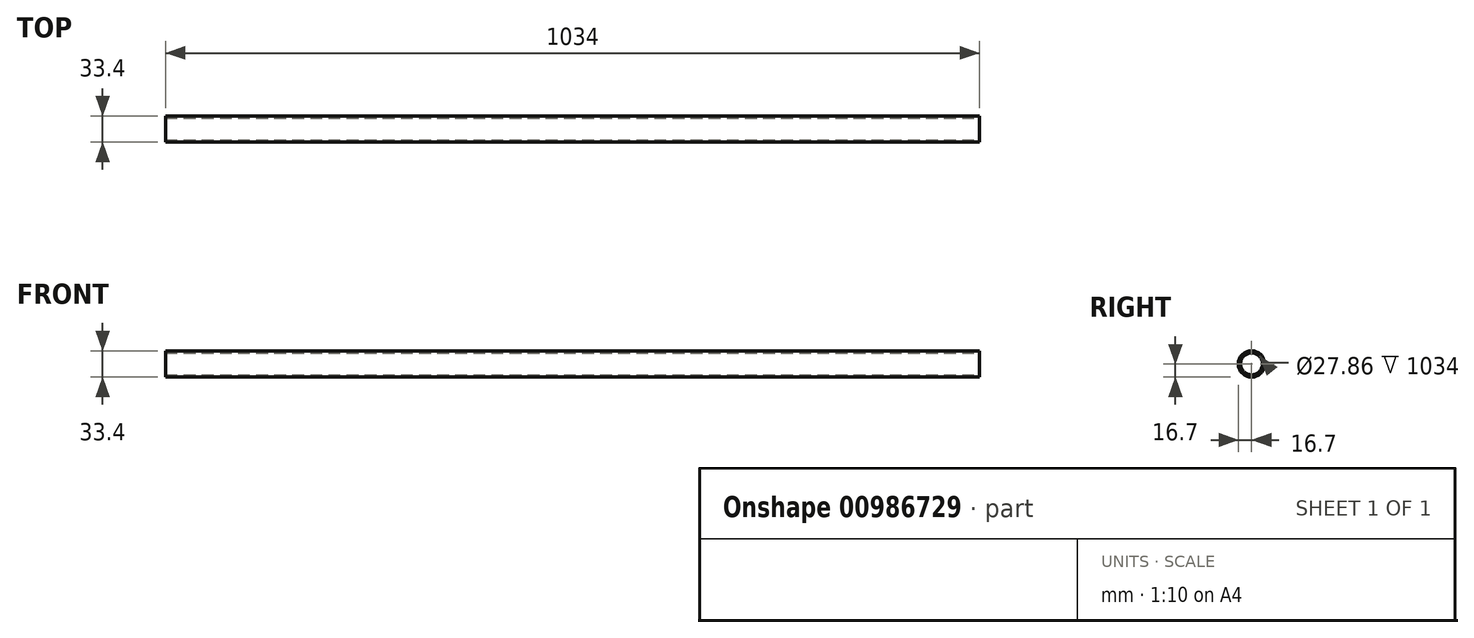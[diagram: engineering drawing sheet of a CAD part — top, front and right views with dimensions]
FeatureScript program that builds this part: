
annotation { "Feature Type Name" : "Feature", "Feature Type Description" : "" }
export const myFeature = defineFeature(function(context is Context, id is Id, definition is map)
    precondition{}
    {
        {
            var Q0;
            Q0=qCreatedBy(makeId("Front.planeOp"),FACE);
            var sketch = newSketch(context, id + "F0", { "sketchPlane" : qUnion([Q0])});
            skLineSegment(sketch, "E0", {"start": v(0, 0) * mm, "end": v(1034, 0) * mm});
            skSolve(sketch);
        }
        {
            var Q0;
            Q0=qCreatedBy(makeId("Right.planeOp"),FACE);
            var sketch = newSketch(context, id + "F1", { "sketchPlane" : qUnion([Q0])});
            skCircle(sketch, "E1", {"center": v(0, 0) * mm, "radius": 16.7 * mm});
            skCircle(sketch, "E2.0", {"center": v(0, 0) * mm, "radius": 13.93 * mm});
            skSolve(sketch);
        }
        {
            var Q0;
            Q0=makeQuery(id+"F1.imprint","IMPRINT",FACE,{"disambiguationData":[TD([[makeQuery(id+"F1.imprint","IMPRINT",EDGE,{"derivedFrom":sQuery(id+"F1.wireOp",EDGE,"E1")}),1.0]])]});
            var Q1;
            Q1=sQuery(id+"F0.wireOp",EDGE,"E0");
            sweep(context, id + "F2", {"profiles" : qUnion([Q0]), "path" : qUnion([Q1])});
        }
    });
